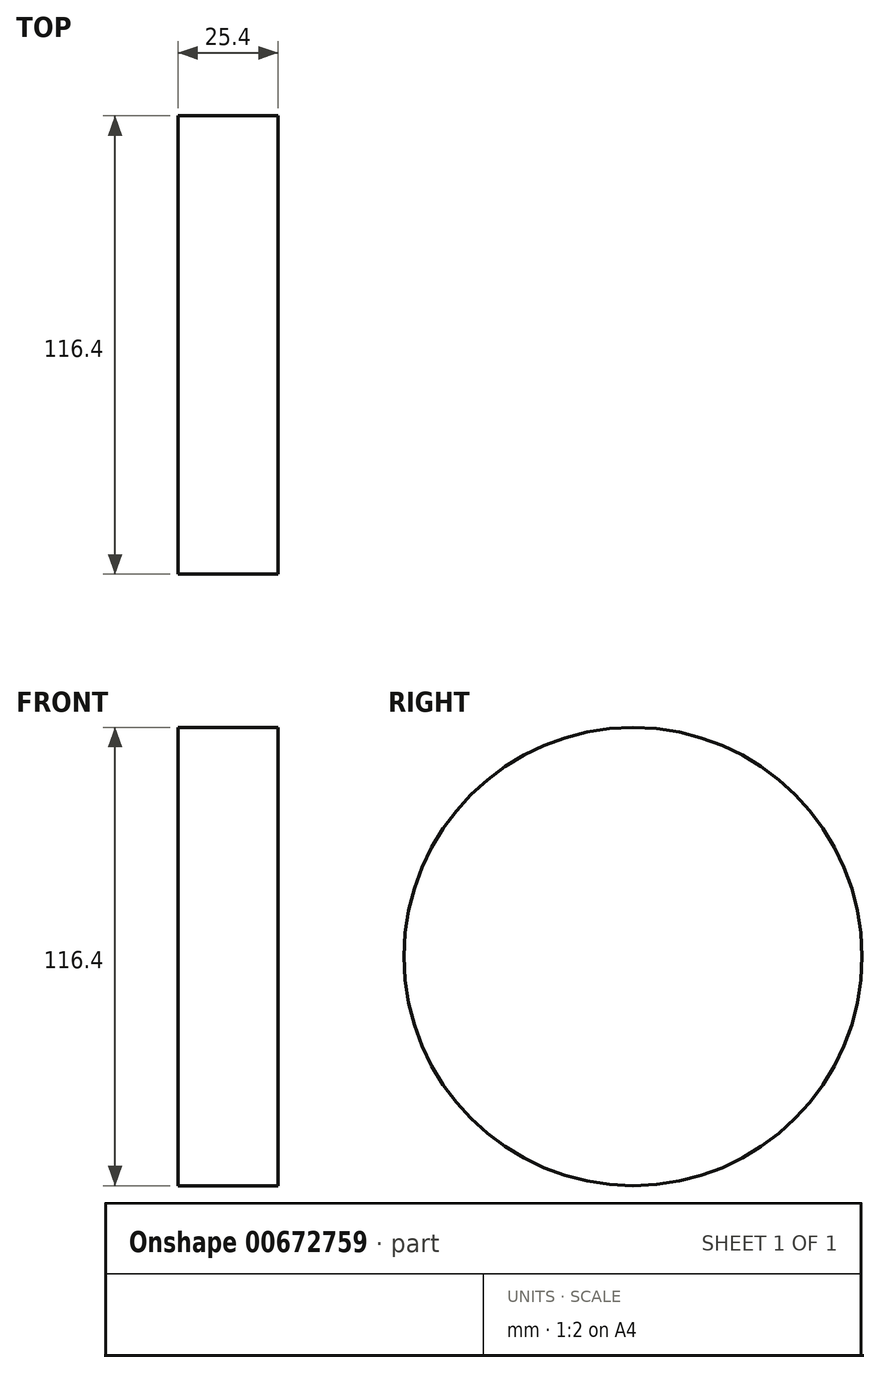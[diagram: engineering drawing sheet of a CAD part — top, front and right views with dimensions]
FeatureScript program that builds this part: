
annotation { "Feature Type Name" : "Feature", "Feature Type Description" : "" }
export const myFeature = defineFeature(function(context is Context, id is Id, definition is map)
    precondition{}
    {
        {
            var Q0;
            Q0=qCreatedBy(makeId("Right.planeOp"),FACE);
            var sketch = newSketch(context, id + "F0", { "sketchPlane" : qUnion([Q0])});
            skCircle(sketch, "E0", {"center": v(0, -35.8) * mm, "radius": 58.2 * mm});
            skSolve(sketch);
        }
        {
            var Q0;
            Q0=qCreatedBy(makeId("Top.planeOp"),FACE);
            var sketch = newSketch(context, id + "F1", { "sketchPlane" : qUnion([Q0])});
            skCircle(sketch, "E1", {"center": v(39.24, 38.14) * mm, "radius": 36.92 * mm});
            skSolve(sketch);
        }
        {
            var Q0;
            Q0=makeQuery(id+"F0.imprint","IMPRINT",FACE,{"disambiguationData":[TD([[makeQuery(id+"F0.imprint","IMPRINT",EDGE,{"derivedFrom":sQuery(id+"F0.wireOp",EDGE,"E0")}),1.0]])]});
            extrude(context, id + "F2", {"entities" : qUnion([Q0]), "depth" : 25.4 * mm, "offsetDistance" : 25.4 * mm});
        }
        {
            var Q0;
            Q0=sQuery(id+"F1.wireOp",EDGE,"E1");
            extrude(context, id + "F3", {"bodyType" : ToolBodyType.SURFACE, "surfaceEntities" : qUnion([Q0]), "oppositeDirection" : true, "depth" : 26.94 * mm, "offsetDistance" : 25.4 * mm});
        }
    });
